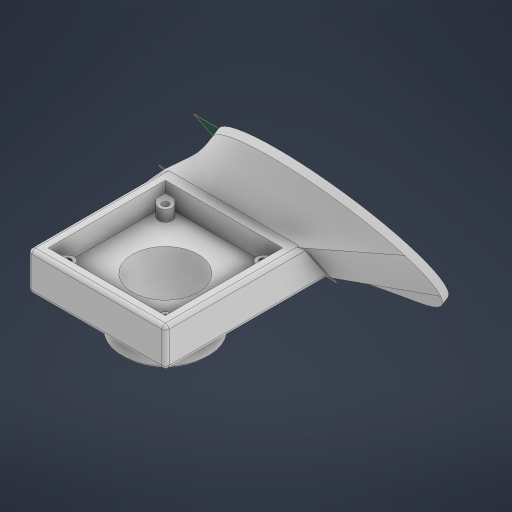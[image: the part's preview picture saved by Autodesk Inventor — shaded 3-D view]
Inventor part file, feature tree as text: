
AUTODESK INVENTOR PART (.ipt)
format: ipt  version: 2023 (Build 270158000, 158)  size: 488,960 bytes
history: native  units: in
note: dims shown in document units (in); Inventor stores cm internally (conversion verified against a paired STEP export)
features: sketch x9, extrude x6, hole x3, plane x2, fillet x2, chamfer x2, projected_geometry x2, other x2, loft x1
ambient origin geometry x8: Origin, YZ Plane, XZ Plane, XY Plane, X Axis, Y Axis, Z Axis, Center Point
bodies: Solid1 (feature_tree)
feature tree (29):
  extrude  "Extrusion1"  Depth=0.525in
  extrude  "Extrusion2"  Depth=0.3848in
  plane  "Work Plane1"
  extrude  "Extrusion3"  Depth=0.6in
  loft  "Loft1"
  extrude  "Extrusion4"  Depth=1.6in
  hole  "Hole1"  [1 undecoded]
  extrude  "Extrusion5"  Depth=0.1839in
  extrude  "Extrusion6"  Depth=0.15in TaperAngle=0.0deg
  hole  "Hole2"  [1 undecoded]
  plane  "Work Plane2"
  hole  "Hole3"  [1 undecoded]
  fillet  "Fillet1"  [1 undecoded]
  chamfer  "Chamfer1"  Distance=0.3in
  fillet  "Fillet2"  Radius=0.2in
  chamfer  "Chamfer2"  Distance=0.05in
  sketch  "Sketch1"  dims[d0=1.875in d1=0.525in]
  sketch  "Sketch2"  dims[d2=1.875in d3=0.0in d4=0.3848in]
  sketch  "Sketch3"  dims[d5=1.875in d6=0.0in d7=0.6in]
  sketch  "Sketch4"  dims[d9=2.75in d10=0.1in d11=0.0in]
  projected_geometry  "Projected Loop1"
  sketch  "Sketch5"  dims[d14=0.0in d15=90.0deg d16=1.6in]
  sketch  "Sketch6"  dims[d17=0.3in d18=0.0in]
  sketch  "Sketch7"  dims[d19=0.9in d20=0.75in d21=0.119in d22=0.25in d23=0.6871in d24=1.0in d25=0.8108in d26=1.1875in]
  projected_geometry  "Projected Loop2"
  sketch  "Sketch8"  dims[d27=0.5in d28=0.0in d29=0.1839in]
  sketch  "Sketch9"  dims[d30=1.3386in d31=0.15in d32=0.0in d33=0.094in d34=0.75in d35=0.251in d36=0.15in d37=0.6871in d38=1.0in d39=0.8108in d40=0.9792in d41=0.9792in d42=45.0deg d43=0.3in d44=0.2in d45=0.177in d46=0.75in d47=0.313in d48=0.45in d49=0.5635in d50=1.0in d51=0.8108in d52=0.05in d53=0.05in d54=0.125in d55=45.0deg d56=0.0625in d61=0.0312in d62=0.125in d63=45.0deg d64=2.75in d65=0.0in d66=90.0deg]
  other  "Edges2"
  other  "Edges3"
note: 4 required parameter values undecoded (feature->parameter linkage not recoverable at this tier; creation-order binding heuristic only, values carry confidence <= 0.55)
